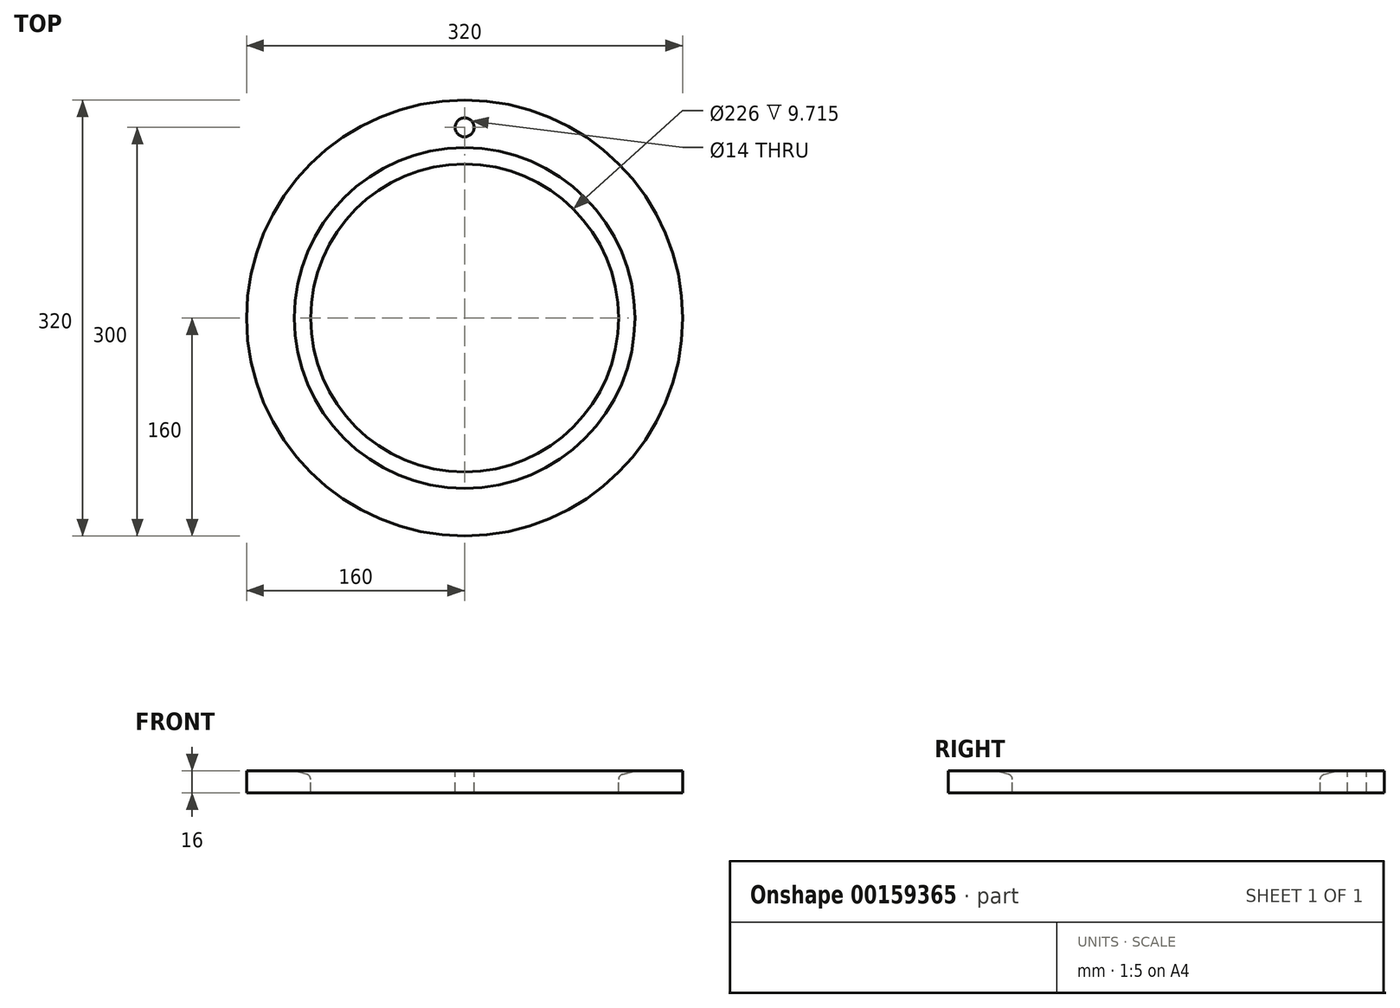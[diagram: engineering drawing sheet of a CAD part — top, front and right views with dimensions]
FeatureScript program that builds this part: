
annotation { "Feature Type Name" : "Feature", "Feature Type Description" : "" }
export const myFeature = defineFeature(function(context is Context, id is Id, definition is map)
    precondition{}
    {
        {
            var Q0;
            Q0=qCreatedBy(makeId("Right.planeOp"),FACE);
            var sketch = newSketch(context, id + "F0", { "sketchPlane" : qUnion([Q0])});
            skLineSegment(sketch, "E0", {"start": v(0, 168.9) * mm, "end": v(0, -172.63) * mm, "construction": true});
            skLineSegment(sketch, "E1", {"start": v(-163.9, 0) * mm, "end": v(166.4, 0) * mm, "construction": true});
            skLineSegment(sketch, "E2.bottom", {"start": v(125, 16) * mm, "end": v(160, 16) * mm});
            skLineSegment(sketch, "E2.top", {"start": v(113, 0) * mm, "end": v(160, 0) * mm});
            skLineSegment(sketch, "E2.right", {"start": v(160, 16) * mm, "end": v(160, 0) * mm});
            skPoint(sketch, "E3", {"position": v(125, 16) * mm});
            skLineSegment(sketch, "E4", {"start": v(113, 0) * mm, "end": v(113, 9.72) * mm});
            skLineSegment(sketch, "E5", {"start": v(125, 16) * mm, "end": v(115.96, 13.58) * mm});
            skPoint(sketch, "E6.visualSharp", {"position": v(113, 12.78) * mm});
            skArc(sketch, "E6.filletArc", {"start": v(115.96, 13.58) * mm, "mid": v(113.83, 12.15) * mm, "end": v(113, 9.72) * mm});
            skSolve(sketch);
        }
        {
            var Q0;
            Q0=makeQuery(id+"F0.imprint","IMPRINT",FACE,{"disambiguationData":[TD([[makeQuery(id+"F0.imprint","IMPRINT",EDGE,{"derivedFrom":sQuery(id+"F0.wireOp",EDGE,"E2.bottom")}),-1.0]])]});
            var Q1;
            Q1=sQuery(id+"F0.wireOp",EDGE,"E0");
            revolve(context, id + "F1", {"entities" : qUnion([Q0]), "axis" : qUnion([Q1]), "revolveType" : RevolveType.FULL});
        }
        {
            var Q0;
            Q0=makeQuery(id+"F1.opRevolve","SWEPT_FACE",FACE,{"disambiguationData":[OSD([sQuery(id+"F0.wireOp",EDGE,"E2.bottom")])]});
            var sketch = newSketch(context, id + "F2", { "sketchPlane" : qUnion([Q0])});
            skCircle(sketch, "E7", {"center": v(0, 140) * mm, "radius": 7 * mm});
            skCircle(sketch, "E8", {"center": v(0, 0) * mm, "radius": 140 * mm, "construction": true});
            skLineSegment(sketch, "E9", {"start": v(0, 0) * mm, "end": v(0, 140) * mm, "construction": true});
            skSolve(sketch);
        }
        {
            var Q0;
            Q0=makeQuery(id+"F2.imprint","IMPRINT",FACE,{"disambiguationData":[TD([[makeQuery(id+"F2.imprint","IMPRINT",EDGE,{"derivedFrom":sQuery(id+"F2.wireOp",EDGE,"E7")}),1.0]])]});
            extrude(context, id + "F3", {"entities" : qUnion([Q0]), "operationType" : NewBodyOperationType.REMOVE, "oppositeDirection" : true, "depth" : 25 * mm});
        }
        {
            var Q0;
            Q0=qCreatedBy(makeId("Right.planeOp"),FACE);
            var sketch = newSketch(context, id + "F4", { "sketchPlane" : qUnion([Q0])});
            skLineSegment(sketch, "E10", {"start": v(0, -31.23) * mm, "end": v(0, 54.88) * mm, "construction": true});
            skSolve(sketch);
        }
    });
